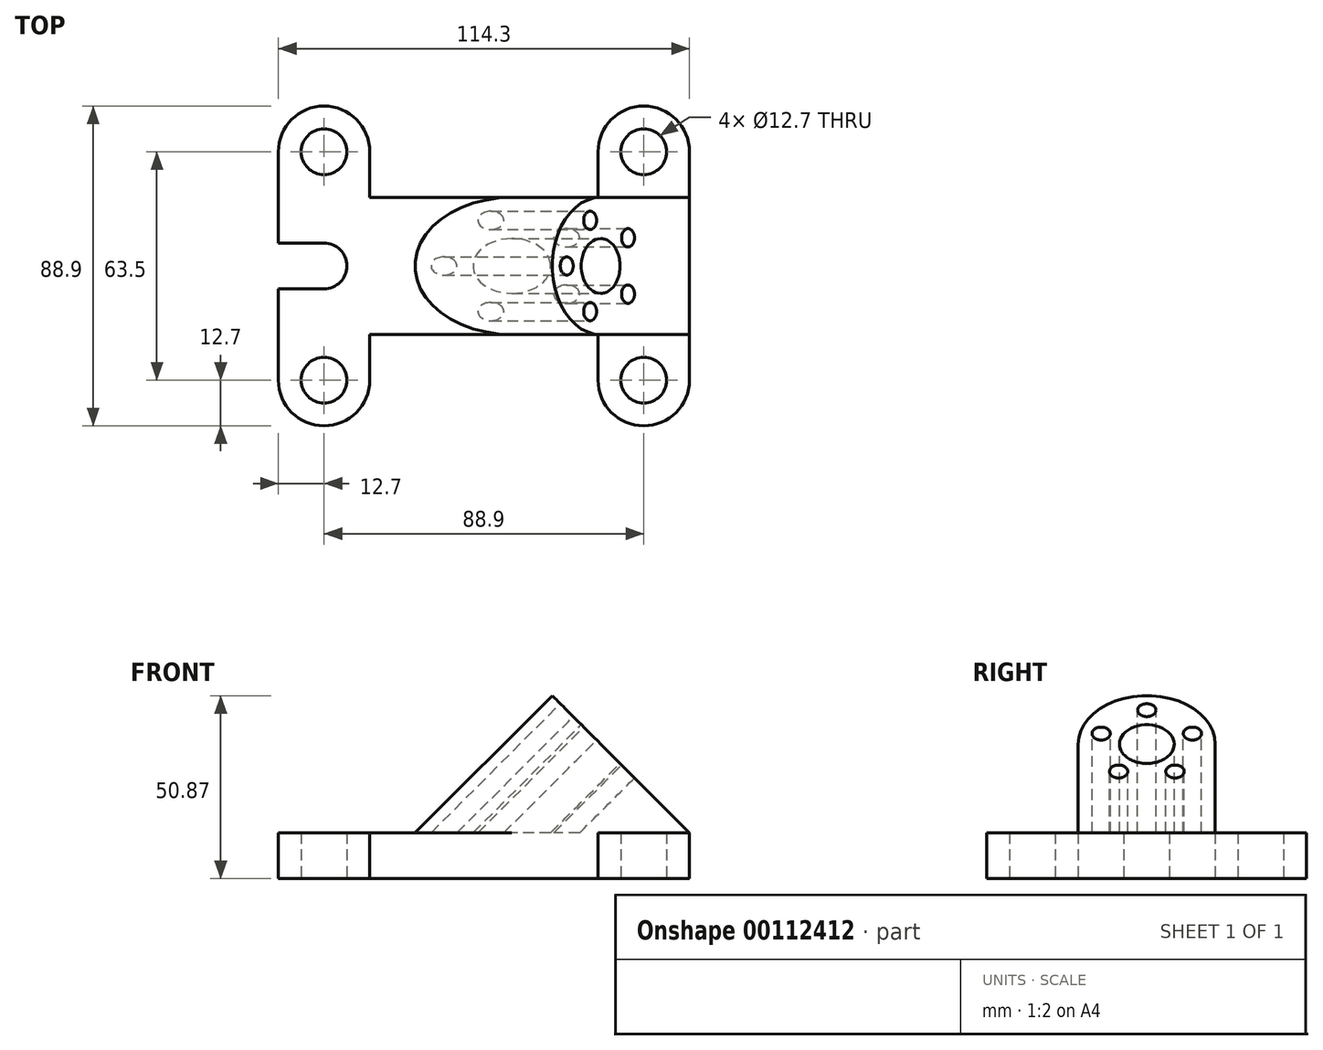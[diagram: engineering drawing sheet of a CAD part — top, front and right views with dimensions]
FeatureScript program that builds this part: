
annotation { "Feature Type Name" : "Feature", "Feature Type Description" : "" }
export const myFeature = defineFeature(function(context is Context, id is Id, definition is map)
    precondition{}
    {
        {
            var Q0;
            Q0=qCreatedBy(makeId("Top.planeOp"),FACE);
            var sketch = newSketch(context, id + "F0", { "sketchPlane" : qUnion([Q0])});
            skArc(sketch, "E0", {"start": v(0, -6.35) * mm, "mid": v(6.35, 0) * mm, "end": v(0, 6.35) * mm});
            skLineSegment(sketch, "E1", {"start": v(0, 6.35) * mm, "end": v(-12.7, 6.35) * mm});
            skLineSegment(sketch, "E2", {"start": v(0, -6.35) * mm, "end": v(-12.7, -6.35) * mm});
            skLineSegment(sketch, "E3", {"start": v(-12.7, -6.35) * mm, "end": v(-12.7, -31.75) * mm});
            skLineSegment(sketch, "E4", {"start": v(12.7, -31.75) * mm, "end": v(12.7, -19.05) * mm});
            skLineSegment(sketch, "E5", {"start": v(12.7, -19.05) * mm, "end": v(101.6, -19.05) * mm});
            skLineSegment(sketch, "E6", {"start": v(101.6, -19.05) * mm, "end": v(101.6, -31.75) * mm});
            skLineSegment(sketch, "E7", {"start": v(76.2, -19.05) * mm, "end": v(76.2, -31.75) * mm});
            skArc(sketch, "E8", {"start": v(76.2, -31.75) * mm, "mid": v(88.9, -44.45) * mm, "end": v(101.6, -31.75) * mm});
            skLineSegment(sketch, "E9", {"start": v(101.6, -19.05) * mm, "end": v(101.6, 19.05) * mm});
            skLineSegment(sketch, "E10", {"start": v(101.6, 19.05) * mm, "end": v(12.7, 19.05) * mm});
            skLineSegment(sketch, "E11", {"start": v(101.6, 19.05) * mm, "end": v(101.6, 31.75) * mm});
            skLineSegment(sketch, "E12", {"start": v(76.2, 19.05) * mm, "end": v(76.2, 31.75) * mm});
            skArc(sketch, "E13", {"start": v(101.6, 31.75) * mm, "mid": v(88.9, 44.45) * mm, "end": v(76.2, 31.75) * mm});
            skLineSegment(sketch, "E14", {"start": v(12.7, 19.05) * mm, "end": v(12.7, 31.75) * mm});
            skLineSegment(sketch, "E15", {"start": v(-12.7, 6.35) * mm, "end": v(-12.7, 31.75) * mm});
            skArc(sketch, "E16", {"start": v(12.7, 31.75) * mm, "mid": v(0, 44.45) * mm, "end": v(-12.7, 31.75) * mm});
            skCircle(sketch, "E17", {"center": v(0, 31.75) * mm, "radius": 6.35 * mm});
            skCircle(sketch, "E18", {"center": v(0, -31.75) * mm, "radius": 6.35 * mm});
            skCircle(sketch, "E19", {"center": v(88.9, 31.75) * mm, "radius": 6.35 * mm});
            skCircle(sketch, "E20", {"center": v(88.9, -31.75) * mm, "radius": 6.35 * mm});
            skLineSegment(sketch, "E21", {"start": v(0, 0) * mm, "end": v(101.6, 0) * mm, "construction": true});
            skArc(sketch, "E22", {"start": v(-12.7, -31.75) * mm, "mid": v(0, -44.45) * mm, "end": v(12.7, -31.75) * mm});
            skLineSegment(sketch, "E23", {"start": v(76.2, 19.05) * mm, "end": v(76.2, -19.05) * mm, "construction": true});
            skSolve(sketch);
        }
        {
            var Q0;
            Q0 = qSketchRegion(id + "F0", true);
            var Q1;
            Q1=sQuery(id+"F0.wireOp",EDGE,"E19");
            var Q2;
            Q2=sQuery(id+"F0.wireOp",EDGE,"E17");
            var Q3;
            Q3=sQuery(id+"F0.wireOp",EDGE,"E13");
            var Q4;
            Q4=sQuery(id+"F0.wireOp",EDGE,"E15");
            var Q5;
            Q5=sQuery(id+"F0.wireOp",EDGE,"E0");
            var Q6;
            Q6=sQuery(id+"F0.wireOp",EDGE,"E22");
            var Q7;
            Q7=sQuery(id+"F0.wireOp",EDGE,"E1");
            var Q8;
            Q8=sQuery(id+"F0.wireOp",EDGE,"E2");
            var Q9;
            Q9=sQuery(id+"F0.wireOp",EDGE,"E20");
            var Q10;
            Q10=sQuery(id+"F0.wireOp",EDGE,"E3");
            var Q11;
            Q11=sQuery(id+"F0.wireOp",EDGE,"E18");
            var Q12;
            Q12=sQuery(id+"F0.wireOp",EDGE,"E5");
            var Q13;
            Q13=sQuery(id+"F0.wireOp",EDGE,"E16");
            var Q14;
            Q14=sQuery(id+"F0.wireOp",EDGE,"E8");
            var Q15;
            Q15=sQuery(id+"F0.wireOp",EDGE,"E10");
            var Q16;
            Q16=sQuery(id+"F0.wireOp",EDGE,"E9");
            var Q17;
            Q17=sQuery(id+"F0.wireOp",EDGE,"E14");
            var Q18;
            Q18=sQuery(id+"F0.wireOp",EDGE,"E4");
            var Q19;
            Q19=sQuery(id+"F0.wireOp",EDGE,"E6");
            var Q20;
            Q20=sQuery(id+"F0.wireOp",EDGE,"E7");
            var Q21;
            Q21=sQuery(id+"F0.wireOp",EDGE,"E11");
            var Q22;
            Q22=sQuery(id+"F0.wireOp",EDGE,"E12");
            extrude(context, id + "F1", {"entities" : qUnion([Q0]), "surfaceEntities" : qUnion([Q1, Q2, Q3, Q4, Q5, Q6, Q7, Q8, Q9, Q10, Q11, Q12, Q13, Q14, Q15, Q16, Q17, Q18, Q19, Q20, Q21, Q22]), "depth" : 12.7 * mm});
        }
        {
            var Q0;
            Q0=makeQuery(id+"F1.opExtrude","CAP_FACE",FACE,{"disambiguationData":[OSD([sQuery(id+"F0.wireOp",EDGE,"E0"),sQuery(id+"F0.wireOp",EDGE,"E1"),sQuery(id+"F0.wireOp",EDGE,"E2"),sQuery(id+"F0.wireOp",EDGE,"E3"),sQuery(id+"F0.wireOp",EDGE,"E4"),sQuery(id+"F0.wireOp",EDGE,"E5"),sQuery(id+"F0.wireOp",EDGE,"E6"),sQuery(id+"F0.wireOp",EDGE,"E7"),sQuery(id+"F0.wireOp",EDGE,"E8"),sQuery(id+"F0.wireOp",EDGE,"E9"),sQuery(id+"F0.wireOp",EDGE,"E10"),sQuery(id+"F0.wireOp",EDGE,"E11"),sQuery(id+"F0.wireOp",EDGE,"E12"),sQuery(id+"F0.wireOp",EDGE,"E13"),sQuery(id+"F0.wireOp",EDGE,"E14"),sQuery(id+"F0.wireOp",EDGE,"E15"),sQuery(id+"F0.wireOp",EDGE,"E16"),sQuery(id+"F0.wireOp",EDGE,"E17"),sQuery(id+"F0.wireOp",EDGE,"E18"),sQuery(id+"F0.wireOp",EDGE,"E19"),sQuery(id+"F0.wireOp",EDGE,"E20"),sQuery(id+"F0.wireOp",EDGE,"E22")])],"isStart":false});
            var Q1;
            Q1=makeQuery(id+"F1.opExtrude","CAP_EDGE",EDGE,{"disambiguationData":[OSD([sQuery(id+"F0.wireOp",EDGE,"E6"),sQuery(id+"F0.wireOp",EDGE,"E9"),sQuery(id+"F0.wireOp",EDGE,"E11")])],"isStart":false});
            cPlane(context, id + "F2", {"entities" : qUnion([Q0, Q1]), "cplaneType" : CPlaneType.LINE_ANGLE, "offset" : 25.4 * mm, "angle" : 135 * degree, "width" : 152.4 * mm, "height" : 152.4 * mm});
        }
        {
            var Q0;
            Q0=qCreatedBy(id+"F2.planeOp",FACE);
            var sketch = newSketch(context, id + "F3", { "sketchPlane" : qUnion([Q0])});
            skLineSegment(sketch, "E24", {"start": v(-19.05, -62.86) * mm, "end": v(-19.05, -27.94) * mm});
            skLineSegment(sketch, "E25", {"start": v(-19.05, -62.86) * mm, "end": v(19.05, -62.86) * mm});
            skLineSegment(sketch, "E26", {"start": v(19.05, -62.86) * mm, "end": v(19.05, -27.94) * mm});
            skArc(sketch, "E27", {"start": v(19.05, -27.94) * mm, "mid": v(0, -8.89) * mm, "end": v(-19.05, -27.94) * mm});
            skCircle(sketch, "E28", {"center": v(0, -27.94) * mm, "radius": 7.62 * mm});
            skCircle(sketch, "E29", {"center": v(0, -14.6) * mm, "radius": 2.54 * mm});
            skLineSegment(sketch, "E30", {"start": v(0, -8.89) * mm, "end": v(0, -20.32) * mm, "construction": true});
            skCircle(sketch, "E31.1.0", {"center": v(-12.68, -23.82) * mm, "radius": 2.54 * mm});
            skCircle(sketch, "E31.2.0", {"center": v(-7.84, -38.73) * mm, "radius": 2.54 * mm});
            skCircle(sketch, "E31.3.0", {"center": v(7.84, -38.73) * mm, "radius": 2.54 * mm});
            skCircle(sketch, "E31.4.0", {"center": v(12.68, -23.82) * mm, "radius": 2.54 * mm});
            skSolve(sketch);
        }
        {
            var Q0;
            Q0 = qSketchRegion(id + "F3", true);
            extrude(context, id + "F4", {"entities" : qUnion([Q0]), "operationType" : NewBodyOperationType.ADD, "endBound" : BoundingType.UP_TO_NEXT, "oppositeDirection" : true, "depth" : 25.4 * mm});
        }
    });
